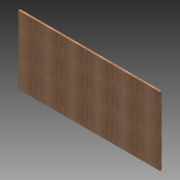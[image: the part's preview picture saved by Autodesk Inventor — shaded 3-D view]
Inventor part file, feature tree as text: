
AUTODESK INVENTOR PART (.ipt)
format: ipt  version: 2013 (Build 170138000, 138)  size: 88,064 bytes
history: native  units: in
note: dims shown in document units (in); Inventor stores cm internally (conversion verified against a paired STEP export)
features: extrude x1, sketch x1
ambient origin geometry x8: Origin, YZ Plane, XZ Plane, XY Plane, X Axis, Y Axis, Z Axis, Center Point
bodies: Solid1 (feature_tree)
feature tree (2):
  extrude  "Extrusion1"  Depth=27.0in
  sketch  "Sketch1"  dims[d0=56.0in d1=27.0in d2=0.75in d3=0.0in]
